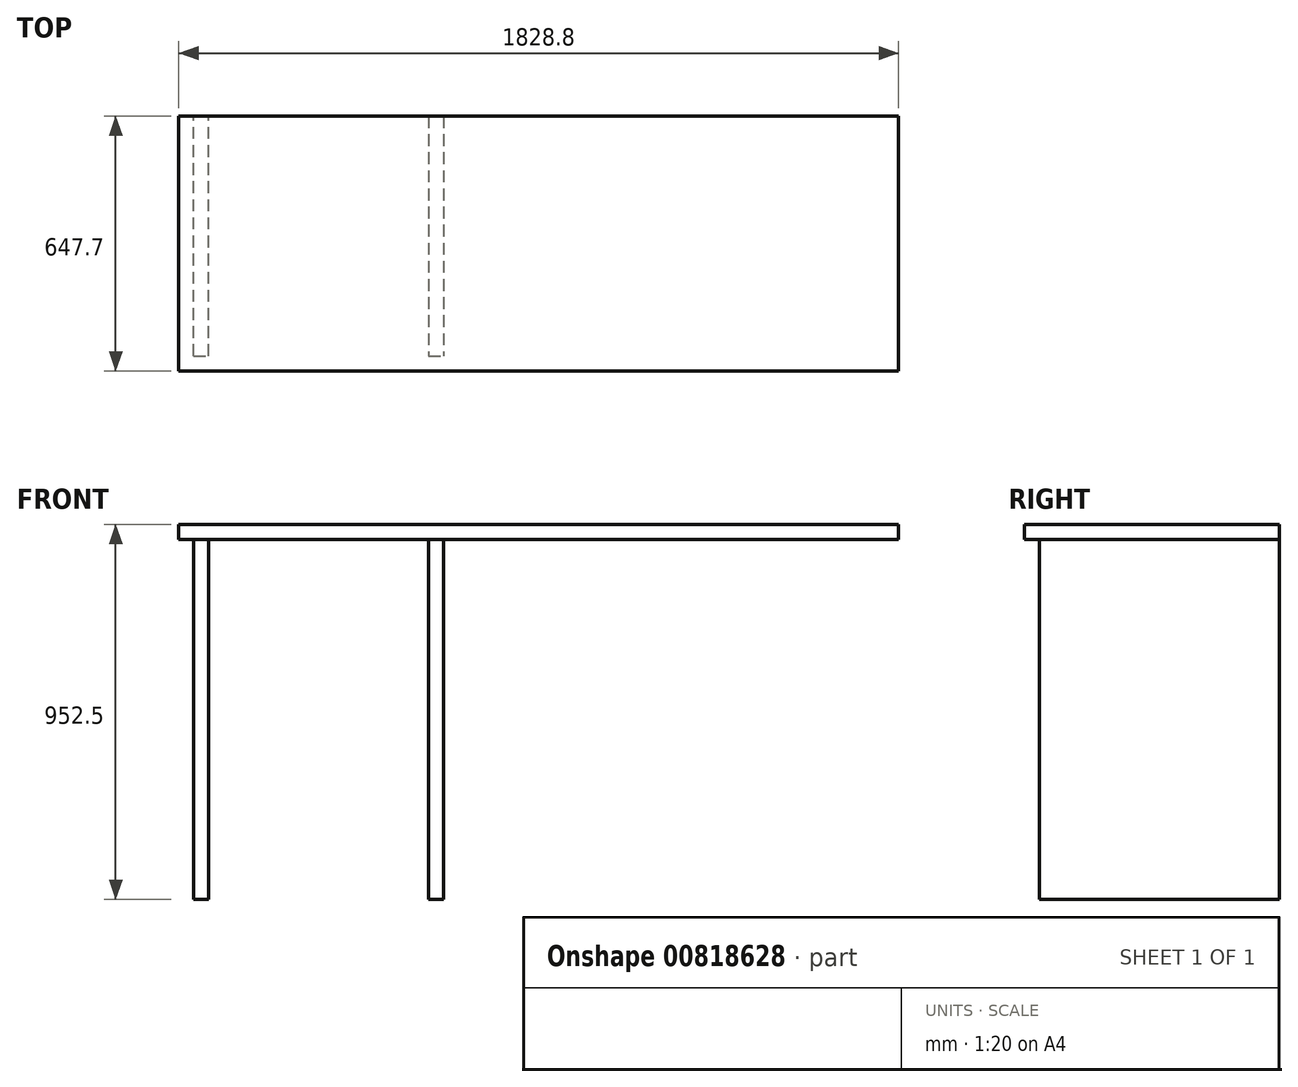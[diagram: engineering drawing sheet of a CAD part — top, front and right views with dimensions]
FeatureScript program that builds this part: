
annotation { "Feature Type Name" : "Feature", "Feature Type Description" : "" }
export const myFeature = defineFeature(function(context is Context, id is Id, definition is map)
    precondition{}
    {
        {
            var Q0;
            Q0=qCreatedBy(makeId("Top.planeOp"),FACE);
            var sketch = newSketch(context, id + "F0", { "sketchPlane" : qUnion([Q0])});
            skLineSegment(sketch, "E0.bottom", {"start": v(914.4, -323.85) * mm, "end": v(-914.4, -323.85) * mm});
            skLineSegment(sketch, "E0.top", {"start": v(914.4, 323.85) * mm, "end": v(-914.4, 323.85) * mm});
            skLineSegment(sketch, "E0.left", {"start": v(914.4, -323.85) * mm, "end": v(914.4, 323.85) * mm});
            skLineSegment(sketch, "E0.right", {"start": v(-914.4, -323.85) * mm, "end": v(-914.4, 323.85) * mm});
            skPoint(sketch, "E0.middle", {"position": v(0, 0) * mm});
            skLineSegment(sketch, "E1.bottom", {"start": v(-914.4, -273.05) * mm, "end": v(914.4, -273.05) * mm});
            skLineSegment(sketch, "E1.top", {"start": v(-914.4, -254) * mm, "end": v(914.4, -254) * mm});
            skLineSegment(sketch, "E1.left", {"start": v(-914.4, -273.05) * mm, "end": v(-914.4, -254) * mm});
            skLineSegment(sketch, "E1.right", {"start": v(914.4, -273.05) * mm, "end": v(914.4, -254) * mm});
            skLineSegment(sketch, "E2.bottom", {"start": v(-914.4, -50.8) * mm, "end": v(914.4, -50.8) * mm});
            skLineSegment(sketch, "E2.top", {"start": v(-914.4, -69.85) * mm, "end": v(914.4, -69.85) * mm});
            skLineSegment(sketch, "E2.left", {"start": v(-914.4, -50.8) * mm, "end": v(-914.4, -69.85) * mm});
            skLineSegment(sketch, "E2.right", {"start": v(914.4, -50.8) * mm, "end": v(914.4, -69.85) * mm});
            skLineSegment(sketch, "E3.bottom", {"start": v(-876.3, -285.75) * mm, "end": v(-838.2, -285.75) * mm});
            skLineSegment(sketch, "E3.top", {"start": v(-876.3, 323.85) * mm, "end": v(-838.2, 323.85) * mm});
            skLineSegment(sketch, "E3.left", {"start": v(-876.3, -285.75) * mm, "end": v(-876.3, 323.85) * mm});
            skLineSegment(sketch, "E3.right", {"start": v(-838.2, -285.75) * mm, "end": v(-838.2, 323.85) * mm});
            skLineSegment(sketch, "E4.bottom", {"start": v(-279.4, 323.85) * mm, "end": v(-241.3, 323.85) * mm});
            skLineSegment(sketch, "E4.top", {"start": v(-279.4, -285.75) * mm, "end": v(-241.3, -285.75) * mm});
            skLineSegment(sketch, "E4.left", {"start": v(-279.4, 323.85) * mm, "end": v(-279.4, -285.75) * mm});
            skLineSegment(sketch, "E4.right", {"start": v(-241.3, 323.85) * mm, "end": v(-241.3, -285.75) * mm});
            skLineSegment(sketch, "E5.bottom", {"start": v(876.3, 323.85) * mm, "end": v(838.2, 323.85) * mm});
            skLineSegment(sketch, "E5.top", {"start": v(876.3, -285.75) * mm, "end": v(838.2, -285.75) * mm});
            skLineSegment(sketch, "E5.left", {"start": v(876.3, 323.85) * mm, "end": v(876.3, -285.75) * mm});
            skLineSegment(sketch, "E5.right", {"start": v(838.2, 323.85) * mm, "end": v(838.2, -285.75) * mm});
            skLineSegment(sketch, "E6.bottom", {"start": v(279.4, 323.85) * mm, "end": v(241.3, 323.85) * mm});
            skLineSegment(sketch, "E6.top", {"start": v(279.4, -285.75) * mm, "end": v(241.3, -285.75) * mm});
            skLineSegment(sketch, "E6.left", {"start": v(279.4, 323.85) * mm, "end": v(279.4, -285.75) * mm});
            skLineSegment(sketch, "E6.right", {"start": v(241.3, 323.85) * mm, "end": v(241.3, -285.75) * mm});
            skSolve(sketch);
        }
        {
            var Q0;
            {var subQ0=sQuery(id+"F0.wireOp",EDGE,"E4.left");var subQ1=sQuery(id+"F0.wireOp",EDGE,"E0.top");var subQ2=makeQuery(id+"F0.imprint","INTERSECT",VERTEX,{"derivedFrom":[subQ1,subQ0]});var subQ3=sQuery(id+"F0.wireOp",EDGE,"E4.right");var subQ4=makeQuery(id+"F0.imprint","INTERSECT",VERTEX,{"derivedFrom":[subQ1,subQ3]});var subQ5=sQuery(id+"F0.wireOp",EDGE,"E2.bottom");var subQ10=sQuery(id+"F0.wireOp",EDGE,"E3.right");var subQ11=makeQuery(id+"F0.imprint","INTERSECT",VERTEX,{"derivedFrom":[subQ1,subQ10]});var subQ18=sQuery(id+"F0.wireOp",EDGE,"E1.top");var subQ19=sQuery(id+"F0.wireOp",EDGE,"E0.left");var subQ20=makeQuery(id+"F0.imprint","INTERSECT",VERTEX,{"derivedFrom":[subQ19,subQ18]});var subQ23=sQuery(id+"F0.wireOp",EDGE,"E5.left");var subQ28=sQuery(id+"F0.wireOp",EDGE,"E0.right");var subQ29=makeQuery(id+"F0.imprint","INTERSECT",VERTEX,{"derivedFrom":[subQ28,subQ18]});var subQ41=sQuery(id+"F0.wireOp",EDGE,"E6.left");var subQ43=sQuery(id+"F0.wireOp",EDGE,"E5.right");var subQ48=sQuery(id+"F0.wireOp",EDGE,"E0.bottom");var subQ53=makeQuery(id+"F0.imprint","INTERSECT",VERTEX,{"derivedFrom":[subQ1,subQ43]});var subQ54=makeQuery(id+"F0.imprint","INTERSECT",VERTEX,{"derivedFrom":[subQ1,subQ23]});var subQ62=makeQuery(id+"F0.imprint","INTERSECT",VERTEX,{"derivedFrom":[subQ1,subQ41]});var subQ68=makeQuery(id+"F0.imprint","INTERSECT",VERTEX,{"derivedFrom":[subQ28,subQ5]});var subQ70=makeQuery(id+"F0.imprint","INTERSECT",VERTEX,{"derivedFrom":[subQ19,subQ5]});var subQ72=makeQuery(id+"F0.imprint","INTERSECT",VERTEX,{"derivedFrom":[subQ1,subQ28]});Q0=qUnion([makeQuery(id+"F0.imprint","IMPRINT",FACE,{"disambiguationData":[TD([[makeQuery(id+"F0.imprint","IMPRINT",EDGE,{"disambiguationData":[TD([[subQ53,-1.0]])],"derivedFrom":subQ1}),1.0]])]}),makeQuery(id+"F0.imprint","IMPRINT",FACE,{"disambiguationData":[TD([[makeQuery(id+"F0.imprint","IMPRINT",EDGE,{"disambiguationData":[TD([[subQ54,1.0]])],"derivedFrom":subQ1}),1.0]])]}),makeQuery(id+"F0.imprint","IMPRINT",FACE,{"disambiguationData":[TD([[makeQuery(id+"F0.imprint","IMPRINT",EDGE,{"disambiguationData":[TD([[subQ2,-1.0]])],"derivedFrom":subQ1}),1.0]])]}),makeQuery(id+"F0.imprint","IMPRINT",FACE,{"disambiguationData":[TD([[makeQuery(id+"F0.imprint","IMPRINT",EDGE,{"disambiguationData":[TD([[subQ72,1.0]])],"derivedFrom":subQ1}),1.0]])]}),makeQuery(id+"F0.imprint","IMPRINT",FACE,{"disambiguationData":[TD([[makeQuery(id+"F0.imprint","IMPRINT",EDGE,{"disambiguationData":[TD([[subQ4,1.0]])],"derivedFrom":subQ1}),1.0]])]}),makeQuery(id+"F0.imprint","IMPRINT",FACE,{"disambiguationData":[TD([[makeQuery(id+"F0.imprint","IMPRINT",EDGE,{"disambiguationData":[TD([[subQ70,1.0]])],"derivedFrom":subQ19}),1.0]])]}),makeQuery(id+"F0.imprint","IMPRINT",FACE,{"disambiguationData":[TD([[makeQuery(id+"F0.imprint","IMPRINT",EDGE,{"disambiguationData":[TD([[subQ68,1.0]])],"derivedFrom":subQ28}),-1.0]])]}),makeQuery(id+"F0.imprint","IMPRINT",FACE,{"disambiguationData":[TD([[makeQuery(id+"F0.imprint","IMPRINT",EDGE,{"disambiguationData":[TD([[subQ62,-1.0]])],"derivedFrom":subQ1}),1.0]])]}),makeQuery(id+"F0.imprint","IMPRINT",FACE,{"disambiguationData":[TD([[makeQuery(id+"F0.imprint","IMPRINT",EDGE,{"disambiguationData":[TD([[subQ20,-1.0]])],"derivedFrom":subQ19}),1.0]])]}),makeQuery(id+"F0.imprint","IMPRINT",FACE,{"disambiguationData":[TD([[makeQuery(id+"F0.imprint","IMPRINT",EDGE,{"disambiguationData":[TD([[subQ29,1.0]])],"derivedFrom":subQ28}),-1.0]])]}),makeQuery(id+"F0.imprint","IMPRINT",FACE,{"disambiguationData":[TD([[makeQuery(id+"F0.imprint","IMPRINT",EDGE,{"disambiguationData":[TD([[subQ53,1.0]])],"derivedFrom":subQ1}),1.0]])]}),makeQuery(id+"F0.imprint","IMPRINT",FACE,{"disambiguationData":[TD([[makeQuery(id+"F0.imprint","IMPRINT",EDGE,{"derivedFrom":subQ48}),-1.0]])]}),makeQuery(id+"F0.imprint","IMPRINT",FACE,{"disambiguationData":[TD([[makeQuery(id+"F0.imprint","IMPRINT",EDGE,{"disambiguationData":[TD([[subQ29,-1.0]])],"derivedFrom":subQ28}),-1.0]])]}),makeQuery(id+"F0.imprint","IMPRINT",FACE,{"disambiguationData":[TD([[makeQuery(id+"F0.imprint","IMPRINT",EDGE,{"disambiguationData":[TD([[subQ20,1.0]])],"derivedFrom":subQ19}),1.0]])]}),makeQuery(id+"F0.imprint","IMPRINT",FACE,{"disambiguationData":[TD([[makeQuery(id+"F0.imprint","IMPRINT",EDGE,{"disambiguationData":[TD([[subQ11,-1.0]])],"derivedFrom":subQ1}),1.0]])]}),makeQuery(id+"F0.imprint","IMPRINT",FACE,{"disambiguationData":[TD([[makeQuery(id+"F0.imprint","IMPRINT",EDGE,{"disambiguationData":[TD([[subQ2,1.0]])],"derivedFrom":subQ1}),1.0]])]})]);}
            var Q1;
            {var subQ0=sQuery(id+"F0.wireOp",EDGE,"E3.right");var subQ1=sQuery(id+"F0.wireOp",EDGE,"E2.bottom");var subQ2=makeQuery(id+"F0.imprint","INTERSECT",VERTEX,{"derivedFrom":[subQ1,subQ0]});Q1=makeQuery(id+"F0.imprint","IMPRINT",FACE,{"disambiguationData":[TD([[makeQuery(id+"F0.imprint","IMPRINT",EDGE,{"disambiguationData":[TD([[subQ2,-1.0]])],"derivedFrom":subQ1}),-1.0]])]});}
            var Q2;
            {var subQ0=sQuery(id+"F0.wireOp",EDGE,"E3.right");var subQ1=sQuery(id+"F0.wireOp",EDGE,"E1.top");var subQ2=makeQuery(id+"F0.imprint","INTERSECT",VERTEX,{"derivedFrom":[subQ1,subQ0]});Q2=makeQuery(id+"F0.imprint","IMPRINT",FACE,{"disambiguationData":[TD([[makeQuery(id+"F0.imprint","IMPRINT",EDGE,{"disambiguationData":[TD([[subQ2,-1.0]])],"derivedFrom":subQ1}),1.0]])]});}
            var Q3;
            {var subQ0=sQuery(id+"F0.wireOp",EDGE,"E4.left");var subQ1=sQuery(id+"F0.wireOp",EDGE,"E1.top");var subQ2=makeQuery(id+"F0.imprint","INTERSECT",VERTEX,{"derivedFrom":[subQ1,subQ0]});Q3=makeQuery(id+"F0.imprint","IMPRINT",FACE,{"disambiguationData":[TD([[makeQuery(id+"F0.imprint","IMPRINT",EDGE,{"disambiguationData":[TD([[subQ2,-1.0]])],"derivedFrom":subQ1}),1.0]])]});}
            var Q4;
            {var subQ0=sQuery(id+"F0.wireOp",EDGE,"E6.right");var subQ1=sQuery(id+"F0.wireOp",EDGE,"E1.top");var subQ2=makeQuery(id+"F0.imprint","INTERSECT",VERTEX,{"derivedFrom":[subQ1,subQ0]});Q4=makeQuery(id+"F0.imprint","IMPRINT",FACE,{"disambiguationData":[TD([[makeQuery(id+"F0.imprint","IMPRINT",EDGE,{"disambiguationData":[TD([[subQ2,1.0]])],"derivedFrom":subQ1}),1.0]])]});}
            var Q5;
            {var subQ0=sQuery(id+"F0.wireOp",EDGE,"E6.left");var subQ1=sQuery(id+"F0.wireOp",EDGE,"E1.top");var subQ2=makeQuery(id+"F0.imprint","INTERSECT",VERTEX,{"derivedFrom":[subQ1,subQ0]});Q5=makeQuery(id+"F0.imprint","IMPRINT",FACE,{"disambiguationData":[TD([[makeQuery(id+"F0.imprint","IMPRINT",EDGE,{"disambiguationData":[TD([[subQ2,-1.0]])],"derivedFrom":subQ1}),1.0]])]});}
            var Q6;
            {var subQ0=sQuery(id+"F0.wireOp",EDGE,"E6.left");var subQ1=sQuery(id+"F0.wireOp",EDGE,"E1.top");var subQ2=makeQuery(id+"F0.imprint","INTERSECT",VERTEX,{"derivedFrom":[subQ1,subQ0]});Q6=makeQuery(id+"F0.imprint","IMPRINT",FACE,{"disambiguationData":[TD([[makeQuery(id+"F0.imprint","IMPRINT",EDGE,{"disambiguationData":[TD([[subQ2,1.0]])],"derivedFrom":subQ1}),1.0]])]});}
            var Q7;
            {var subQ0=sQuery(id+"F0.wireOp",EDGE,"E5.right");var subQ1=sQuery(id+"F0.wireOp",EDGE,"E1.top");var subQ2=makeQuery(id+"F0.imprint","INTERSECT",VERTEX,{"derivedFrom":[subQ1,subQ0]});Q7=makeQuery(id+"F0.imprint","IMPRINT",FACE,{"disambiguationData":[TD([[makeQuery(id+"F0.imprint","IMPRINT",EDGE,{"disambiguationData":[TD([[subQ2,-1.0]])],"derivedFrom":subQ1}),1.0]])]});}
            var Q8;
            {var subQ0=sQuery(id+"F0.wireOp",EDGE,"E6.left");var subQ1=sQuery(id+"F0.wireOp",EDGE,"E2.bottom");var subQ2=makeQuery(id+"F0.imprint","INTERSECT",VERTEX,{"derivedFrom":[subQ1,subQ0]});Q8=makeQuery(id+"F0.imprint","IMPRINT",FACE,{"disambiguationData":[TD([[makeQuery(id+"F0.imprint","IMPRINT",EDGE,{"disambiguationData":[TD([[subQ2,-1.0]])],"derivedFrom":subQ1}),-1.0]])]});}
            var Q9;
            {var subQ0=sQuery(id+"F0.wireOp",EDGE,"E3.right");var subQ1=sQuery(id+"F0.wireOp",EDGE,"E1.top");var subQ2=makeQuery(id+"F0.imprint","INTERSECT",VERTEX,{"derivedFrom":[subQ1,subQ0]});Q9=makeQuery(id+"F0.imprint","IMPRINT",FACE,{"disambiguationData":[TD([[makeQuery(id+"F0.imprint","IMPRINT",EDGE,{"disambiguationData":[TD([[subQ2,1.0]])],"derivedFrom":subQ1}),1.0]])]});}
            var Q10;
            {var subQ0=sQuery(id+"F0.wireOp",EDGE,"E3.left");var subQ1=sQuery(id+"F0.wireOp",EDGE,"E2.bottom");var subQ2=makeQuery(id+"F0.imprint","INTERSECT",VERTEX,{"derivedFrom":[subQ1,subQ0]});Q10=makeQuery(id+"F0.imprint","IMPRINT",FACE,{"disambiguationData":[TD([[makeQuery(id+"F0.imprint","IMPRINT",EDGE,{"disambiguationData":[TD([[subQ2,-1.0]])],"derivedFrom":subQ1}),-1.0]])]});}
            var Q11;
            {var subQ0=sQuery(id+"F0.wireOp",EDGE,"E3.right");var subQ1=sQuery(id+"F0.wireOp",EDGE,"E1.bottom");var subQ2=makeQuery(id+"F0.imprint","INTERSECT",VERTEX,{"derivedFrom":[subQ1,subQ0]});Q11=makeQuery(id+"F0.imprint","IMPRINT",FACE,{"disambiguationData":[TD([[makeQuery(id+"F0.imprint","IMPRINT",EDGE,{"disambiguationData":[TD([[subQ2,1.0]])],"derivedFrom":subQ1}),1.0]])]});}
            var Q12;
            {var subQ5=sQuery(id+"F0.wireOp",EDGE,"E3.bottom");Q12=makeQuery(id+"F0.imprint","IMPRINT",FACE,{"disambiguationData":[TD([[makeQuery(id+"F0.imprint","IMPRINT",EDGE,{"derivedFrom":subQ5}),1.0]])]});}
            var Q13;
            {var subQ0=sQuery(id+"F0.wireOp",EDGE,"E3.right");var subQ1=sQuery(id+"F0.wireOp",EDGE,"E1.bottom");var subQ2=makeQuery(id+"F0.imprint","INTERSECT",VERTEX,{"derivedFrom":[subQ1,subQ0]});Q13=makeQuery(id+"F0.imprint","IMPRINT",FACE,{"disambiguationData":[TD([[makeQuery(id+"F0.imprint","IMPRINT",EDGE,{"disambiguationData":[TD([[subQ2,-1.0]])],"derivedFrom":subQ1}),1.0]])]});}
            var Q14;
            {var subQ0=sQuery(id+"F0.wireOp",EDGE,"E4.right");var subQ1=sQuery(id+"F0.wireOp",EDGE,"E2.bottom");var subQ2=makeQuery(id+"F0.imprint","INTERSECT",VERTEX,{"derivedFrom":[subQ1,subQ0]});Q14=makeQuery(id+"F0.imprint","IMPRINT",FACE,{"disambiguationData":[TD([[makeQuery(id+"F0.imprint","IMPRINT",EDGE,{"disambiguationData":[TD([[subQ2,-1.0]])],"derivedFrom":subQ1}),-1.0]])]});}
            var Q15;
            {var subQ0=sQuery(id+"F0.wireOp",EDGE,"E6.right");var subQ1=sQuery(id+"F0.wireOp",EDGE,"E1.bottom");var subQ2=makeQuery(id+"F0.imprint","INTERSECT",VERTEX,{"derivedFrom":[subQ1,subQ0]});Q15=makeQuery(id+"F0.imprint","IMPRINT",FACE,{"disambiguationData":[TD([[makeQuery(id+"F0.imprint","IMPRINT",EDGE,{"disambiguationData":[TD([[subQ2,1.0]])],"derivedFrom":subQ1}),1.0]])]});}
            var Q16;
            {var subQ0=sQuery(id+"F0.wireOp",EDGE,"E4.left");var subQ1=sQuery(id+"F0.wireOp",EDGE,"E1.bottom");var subQ2=makeQuery(id+"F0.imprint","INTERSECT",VERTEX,{"derivedFrom":[subQ1,subQ0]});Q16=makeQuery(id+"F0.imprint","IMPRINT",FACE,{"disambiguationData":[TD([[makeQuery(id+"F0.imprint","IMPRINT",EDGE,{"disambiguationData":[TD([[subQ2,-1.0]])],"derivedFrom":subQ1}),1.0]])]});}
            var Q17;
            {var subQ5=sQuery(id+"F0.wireOp",EDGE,"E4.top");Q17=makeQuery(id+"F0.imprint","IMPRINT",FACE,{"disambiguationData":[TD([[makeQuery(id+"F0.imprint","IMPRINT",EDGE,{"derivedFrom":subQ5}),1.0]])]});}
            var Q18;
            {var subQ0=sQuery(id+"F0.wireOp",EDGE,"E4.right");var subQ1=sQuery(id+"F0.wireOp",EDGE,"E2.bottom");var subQ2=makeQuery(id+"F0.imprint","INTERSECT",VERTEX,{"derivedFrom":[subQ1,subQ0]});Q18=makeQuery(id+"F0.imprint","IMPRINT",FACE,{"disambiguationData":[TD([[makeQuery(id+"F0.imprint","IMPRINT",EDGE,{"disambiguationData":[TD([[subQ2,1.0]])],"derivedFrom":subQ1}),-1.0]])]});}
            var Q19;
            {var subQ0=sQuery(id+"F0.wireOp",EDGE,"E6.left");var subQ1=sQuery(id+"F0.wireOp",EDGE,"E2.bottom");var subQ2=makeQuery(id+"F0.imprint","INTERSECT",VERTEX,{"derivedFrom":[subQ1,subQ0]});Q19=makeQuery(id+"F0.imprint","IMPRINT",FACE,{"disambiguationData":[TD([[makeQuery(id+"F0.imprint","IMPRINT",EDGE,{"disambiguationData":[TD([[subQ2,1.0]])],"derivedFrom":subQ1}),-1.0]])]});}
            var Q20;
            {var subQ5=sQuery(id+"F0.wireOp",EDGE,"E6.top");Q20=makeQuery(id+"F0.imprint","IMPRINT",FACE,{"disambiguationData":[TD([[makeQuery(id+"F0.imprint","IMPRINT",EDGE,{"derivedFrom":subQ5}),-1.0]])]});}
            var Q21;
            {var subQ0=sQuery(id+"F0.wireOp",EDGE,"E6.left");var subQ1=sQuery(id+"F0.wireOp",EDGE,"E1.bottom");var subQ2=makeQuery(id+"F0.imprint","INTERSECT",VERTEX,{"derivedFrom":[subQ1,subQ0]});Q21=makeQuery(id+"F0.imprint","IMPRINT",FACE,{"disambiguationData":[TD([[makeQuery(id+"F0.imprint","IMPRINT",EDGE,{"disambiguationData":[TD([[subQ2,1.0]])],"derivedFrom":subQ1}),1.0]])]});}
            var Q22;
            {var subQ0=sQuery(id+"F0.wireOp",EDGE,"E6.left");var subQ1=sQuery(id+"F0.wireOp",EDGE,"E1.bottom");var subQ2=makeQuery(id+"F0.imprint","INTERSECT",VERTEX,{"derivedFrom":[subQ1,subQ0]});Q22=makeQuery(id+"F0.imprint","IMPRINT",FACE,{"disambiguationData":[TD([[makeQuery(id+"F0.imprint","IMPRINT",EDGE,{"disambiguationData":[TD([[subQ2,-1.0]])],"derivedFrom":subQ1}),1.0]])]});}
            var Q23;
            {var subQ0=sQuery(id+"F0.wireOp",EDGE,"E5.right");var subQ1=sQuery(id+"F0.wireOp",EDGE,"E2.bottom");var subQ2=makeQuery(id+"F0.imprint","INTERSECT",VERTEX,{"derivedFrom":[subQ1,subQ0]});Q23=makeQuery(id+"F0.imprint","IMPRINT",FACE,{"disambiguationData":[TD([[makeQuery(id+"F0.imprint","IMPRINT",EDGE,{"disambiguationData":[TD([[subQ2,-1.0]])],"derivedFrom":subQ1}),-1.0]])]});}
            var Q24;
            {var subQ0=sQuery(id+"F0.wireOp",EDGE,"E5.right");var subQ1=sQuery(id+"F0.wireOp",EDGE,"E1.bottom");var subQ2=makeQuery(id+"F0.imprint","INTERSECT",VERTEX,{"derivedFrom":[subQ1,subQ0]});Q24=makeQuery(id+"F0.imprint","IMPRINT",FACE,{"disambiguationData":[TD([[makeQuery(id+"F0.imprint","IMPRINT",EDGE,{"disambiguationData":[TD([[subQ2,-1.0]])],"derivedFrom":subQ1}),1.0]])]});}
            var Q25;
            {var subQ5=sQuery(id+"F0.wireOp",EDGE,"E5.top");Q25=makeQuery(id+"F0.imprint","IMPRINT",FACE,{"disambiguationData":[TD([[makeQuery(id+"F0.imprint","IMPRINT",EDGE,{"derivedFrom":subQ5}),-1.0]])]});}
            extrude(context, id + "F1", {"entities" : qUnion([Q0, Q1, Q2, Q3, Q4, Q5, Q6, Q7, Q8, Q9, Q10, Q11, Q12, Q13, Q14, Q15, Q16, Q17, Q18, Q19, Q20, Q21, Q22, Q23, Q24, Q25]), "depth" : 38.1 * mm, "offsetDistance" : 25.4 * mm});
        }
        {
            var Q0;
            {var subQ0=sQuery(id+"F0.wireOp",EDGE,"E4.left");var subQ1=sQuery(id+"F0.wireOp",EDGE,"E1.bottom");var subQ2=makeQuery(id+"F0.imprint","INTERSECT",VERTEX,{"derivedFrom":[subQ1,subQ0]});Q0=makeQuery(id+"F0.imprint","IMPRINT",FACE,{"disambiguationData":[TD([[makeQuery(id+"F0.imprint","IMPRINT",EDGE,{"disambiguationData":[TD([[subQ2,-1.0]])],"derivedFrom":subQ1}),1.0]])]});}
            var Q1;
            {var subQ0=sQuery(id+"F0.wireOp",EDGE,"E4.right");var subQ1=sQuery(id+"F0.wireOp",EDGE,"E2.bottom");var subQ2=makeQuery(id+"F0.imprint","INTERSECT",VERTEX,{"derivedFrom":[subQ1,subQ0]});Q1=makeQuery(id+"F0.imprint","IMPRINT",FACE,{"disambiguationData":[TD([[makeQuery(id+"F0.imprint","IMPRINT",EDGE,{"disambiguationData":[TD([[subQ2,1.0]])],"derivedFrom":subQ1}),-1.0]])]});}
            var Q2;
            {var subQ0=sQuery(id+"F0.wireOp",EDGE,"E4.left");var subQ1=sQuery(id+"F0.wireOp",EDGE,"E1.top");var subQ2=makeQuery(id+"F0.imprint","INTERSECT",VERTEX,{"derivedFrom":[subQ1,subQ0]});Q2=makeQuery(id+"F0.imprint","IMPRINT",FACE,{"disambiguationData":[TD([[makeQuery(id+"F0.imprint","IMPRINT",EDGE,{"disambiguationData":[TD([[subQ2,-1.0]])],"derivedFrom":subQ1}),1.0]])]});}
            var Q3;
            {var subQ5=sQuery(id+"F0.wireOp",EDGE,"E4.top");Q3=makeQuery(id+"F0.imprint","IMPRINT",FACE,{"disambiguationData":[TD([[makeQuery(id+"F0.imprint","IMPRINT",EDGE,{"derivedFrom":subQ5}),1.0]])]});}
            var Q4;
            {var subQ0=sQuery(id+"F0.wireOp",EDGE,"E4.left");var subQ1=sQuery(id+"F0.wireOp",EDGE,"E0.top");var subQ2=makeQuery(id+"F0.imprint","INTERSECT",VERTEX,{"derivedFrom":[subQ1,subQ0]});Q4=makeQuery(id+"F0.imprint","IMPRINT",FACE,{"disambiguationData":[TD([[makeQuery(id+"F0.imprint","IMPRINT",EDGE,{"disambiguationData":[TD([[subQ2,1.0]])],"derivedFrom":subQ1}),1.0]])]});}
            extrude(context, id + "F2", {"entities" : qUnion([Q0, Q1, Q2, Q3, Q4]), "operationType" : NewBodyOperationType.ADD, "oppositeDirection" : true, "depth" : 914.4 * mm, "offsetDistance" : 25.4 * mm});
        }
        {
            var Q0;
            {var subQ0=sQuery(id+"F0.wireOp",EDGE,"E3.right");var subQ1=sQuery(id+"F0.wireOp",EDGE,"E1.bottom");var subQ2=makeQuery(id+"F0.imprint","INTERSECT",VERTEX,{"derivedFrom":[subQ1,subQ0]});Q0=makeQuery(id+"F0.imprint","IMPRINT",FACE,{"disambiguationData":[TD([[makeQuery(id+"F0.imprint","IMPRINT",EDGE,{"disambiguationData":[TD([[subQ2,1.0]])],"derivedFrom":subQ1}),1.0]])]});}
            var Q1;
            {var subQ0=sQuery(id+"F0.wireOp",EDGE,"E3.right");var subQ1=sQuery(id+"F0.wireOp",EDGE,"E0.top");var subQ2=makeQuery(id+"F0.imprint","INTERSECT",VERTEX,{"derivedFrom":[subQ1,subQ0]});Q1=makeQuery(id+"F0.imprint","IMPRINT",FACE,{"disambiguationData":[TD([[makeQuery(id+"F0.imprint","IMPRINT",EDGE,{"disambiguationData":[TD([[subQ2,-1.0]])],"derivedFrom":subQ1}),1.0]])]});}
            var Q2;
            {var subQ0=sQuery(id+"F0.wireOp",EDGE,"E3.left");var subQ1=sQuery(id+"F0.wireOp",EDGE,"E2.bottom");var subQ2=makeQuery(id+"F0.imprint","INTERSECT",VERTEX,{"derivedFrom":[subQ1,subQ0]});Q2=makeQuery(id+"F0.imprint","IMPRINT",FACE,{"disambiguationData":[TD([[makeQuery(id+"F0.imprint","IMPRINT",EDGE,{"disambiguationData":[TD([[subQ2,-1.0]])],"derivedFrom":subQ1}),-1.0]])]});}
            var Q3;
            {var subQ5=sQuery(id+"F0.wireOp",EDGE,"E3.bottom");Q3=makeQuery(id+"F0.imprint","IMPRINT",FACE,{"disambiguationData":[TD([[makeQuery(id+"F0.imprint","IMPRINT",EDGE,{"derivedFrom":subQ5}),1.0]])]});}
            var Q4;
            {var subQ0=sQuery(id+"F0.wireOp",EDGE,"E3.right");var subQ1=sQuery(id+"F0.wireOp",EDGE,"E1.top");var subQ2=makeQuery(id+"F0.imprint","INTERSECT",VERTEX,{"derivedFrom":[subQ1,subQ0]});Q4=makeQuery(id+"F0.imprint","IMPRINT",FACE,{"disambiguationData":[TD([[makeQuery(id+"F0.imprint","IMPRINT",EDGE,{"disambiguationData":[TD([[subQ2,1.0]])],"derivedFrom":subQ1}),1.0]])]});}
            extrude(context, id + "F3", {"entities" : qUnion([Q0, Q1, Q2, Q3, Q4]), "operationType" : NewBodyOperationType.ADD, "oppositeDirection" : true, "depth" : 914.4 * mm, "offsetDistance" : 25.4 * mm});
        }
    });
